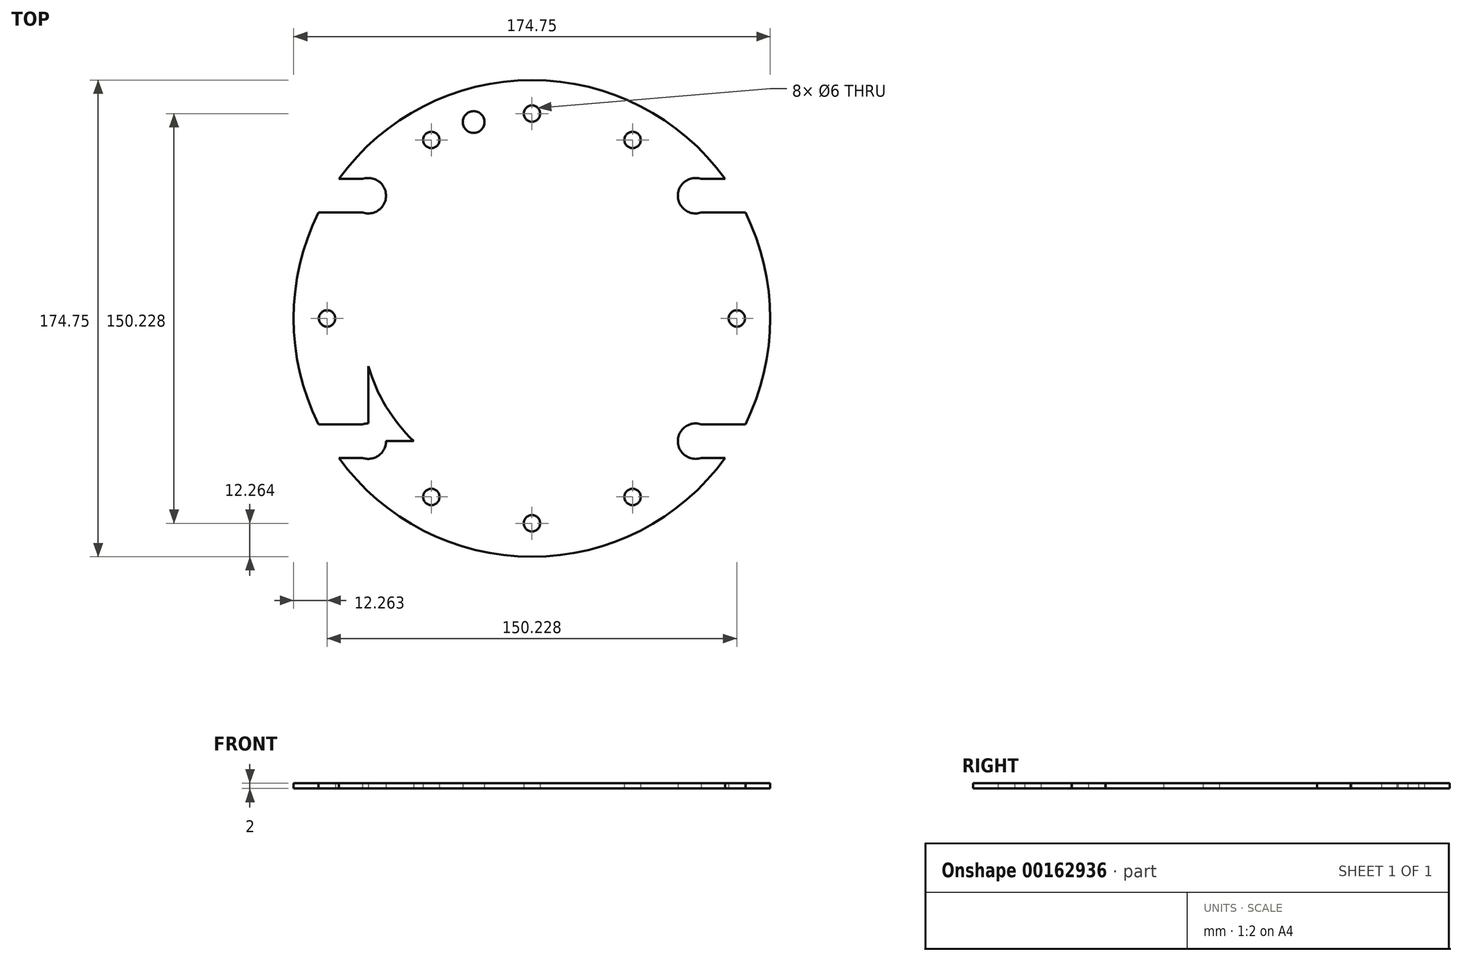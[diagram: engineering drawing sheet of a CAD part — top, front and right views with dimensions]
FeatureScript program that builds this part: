
annotation { "Feature Type Name" : "Feature", "Feature Type Description" : "" }
export const myFeature = defineFeature(function(context is Context, id is Id, definition is map)
    precondition{}
    {
        {
            var Q0;
            Q0=qCreatedBy(makeId("Top.planeOp"),FACE);
            var sketch = newSketch(context, id + "F0", { "sketchPlane" : qUnion([Q0])});
            skLineSegment(sketch, "E0.bottom", {"start": v(60.27, 43.84) * mm, "end": v(-59.73, 43.84) * mm});
            skLineSegment(sketch, "E0.top", {"start": v(60.27, -46.16) * mm, "end": v(-59.73, -46.16) * mm});
            skLineSegment(sketch, "E0.left", {"start": v(60.27, 43.84) * mm, "end": v(60.27, -46.16) * mm});
            skLineSegment(sketch, "E0.right", {"start": v(-59.73, 43.84) * mm, "end": v(-59.73, -46.16) * mm});
            skPoint(sketch, "E0.middle", {"position": v(0.27, -1.16) * mm});
            skCircle(sketch, "E1", {"center": v(60.27, 43.84) * mm, "radius": 6.5 * mm});
            skCircle(sketch, "E2", {"center": v(-59.73, 43.84) * mm, "radius": 6.5 * mm});
            skCircle(sketch, "E3", {"center": v(60.27, -46.16) * mm, "radius": 6.5 * mm});
            skCircle(sketch, "E4", {"center": v(-59.73, -46.16) * mm, "radius": 6.5 * mm});
            skCircle(sketch, "E5", {"center": v(0.27, -1.16) * mm, "radius": 87.38 * mm});
            skLineSegment(sketch, "E6.bottom", {"start": v(58.16, 49.99) * mm, "end": v(62.37, 49.99) * mm});
            skLineSegment(sketch, "E6.top", {"start": v(58.16, 37.69) * mm, "end": v(62.37, 37.69) * mm});
            skLineSegment(sketch, "E6.left", {"start": v(58.16, 49.99) * mm, "end": v(58.16, 37.69) * mm});
            skLineSegment(sketch, "E6.right", {"start": v(62.37, 49.99) * mm, "end": v(62.37, 37.69) * mm});
            skLineSegment(sketch, "E7.bottom", {"start": v(-61.84, 49.99) * mm, "end": v(-57.63, 49.99) * mm});
            skLineSegment(sketch, "E7.top", {"start": v(-61.84, 37.69) * mm, "end": v(-57.63, 37.69) * mm});
            skLineSegment(sketch, "E7.left", {"start": v(-61.84, 49.99) * mm, "end": v(-61.84, 37.69) * mm});
            skLineSegment(sketch, "E7.right", {"start": v(-57.63, 49.99) * mm, "end": v(-57.63, 37.69) * mm});
            skLineSegment(sketch, "E8.bottom", {"start": v(62.37, -40.01) * mm, "end": v(58.16, -40.01) * mm});
            skLineSegment(sketch, "E8.top", {"start": v(62.37, -52.31) * mm, "end": v(58.16, -52.31) * mm});
            skLineSegment(sketch, "E8.left", {"start": v(62.37, -40.01) * mm, "end": v(62.37, -52.31) * mm});
            skLineSegment(sketch, "E8.right", {"start": v(58.16, -40.01) * mm, "end": v(58.16, -52.31) * mm});
            skLineSegment(sketch, "E9.bottom", {"start": v(-61.84, -40.01) * mm, "end": v(-57.63, -40.01) * mm});
            skLineSegment(sketch, "E9.top", {"start": v(-61.84, -52.31) * mm, "end": v(-57.63, -52.31) * mm});
            skLineSegment(sketch, "E9.left", {"start": v(-61.84, -40.01) * mm, "end": v(-61.84, -52.31) * mm});
            skLineSegment(sketch, "E9.right", {"start": v(-57.63, -40.01) * mm, "end": v(-57.63, -52.31) * mm});
            skLineSegment(sketch, "E10.bottom", {"start": v(58.16, -40.01) * mm, "end": v(80.94, -40.01) * mm});
            skLineSegment(sketch, "E10.top", {"start": v(58.16, -52.31) * mm, "end": v(80.94, -52.31) * mm});
            skLineSegment(sketch, "E10.right", {"start": v(80.94, -40.01) * mm, "end": v(80.94, -52.31) * mm});
            skLineSegment(sketch, "E11.bottom", {"start": v(58.16, 49.99) * mm, "end": v(78.53, 49.99) * mm});
            skLineSegment(sketch, "E11.top", {"start": v(58.16, 37.69) * mm, "end": v(78.53, 37.69) * mm});
            skLineSegment(sketch, "E11.right", {"start": v(78.53, 49.99) * mm, "end": v(78.53, 37.69) * mm});
            skLineSegment(sketch, "E12.bottom", {"start": v(-57.63, 49.99) * mm, "end": v(-78, 49.99) * mm});
            skLineSegment(sketch, "E12.top", {"start": v(-57.63, 37.69) * mm, "end": v(-78, 37.69) * mm});
            skLineSegment(sketch, "E12.right", {"start": v(-78, 49.99) * mm, "end": v(-78, 37.69) * mm});
            skLineSegment(sketch, "E13.bottom", {"start": v(-57.63, -40.01) * mm, "end": v(-78, -40.01) * mm});
            skLineSegment(sketch, "E13.top", {"start": v(-57.63, -52.31) * mm, "end": v(-78, -52.31) * mm});
            skLineSegment(sketch, "E13.right", {"start": v(-78, -40.01) * mm, "end": v(-78, -52.31) * mm});
            skCircle(sketch, "E14", {"center": v(0.27, -1.16) * mm, "radius": 62.5 * mm});
            skCircle(sketch, "E15", {"center": v(0.27, 73.95) * mm, "radius": 3 * mm});
            skCircle(sketch, "E16", {"center": v(0.27, -76.28) * mm, "radius": 3 * mm});
            skCircle(sketch, "E17", {"center": v(75.38, -1.16) * mm, "radius": 3 * mm});
            skCircle(sketch, "E18", {"center": v(-74.85, -1.16) * mm, "radius": 3 * mm});
            skCircle(sketch, "E19", {"center": v(-21.11, 70.87) * mm, "radius": 4 * mm});
            skCircle(sketch, "E20", {"center": v(0.27, -1.16) * mm, "radius": 75.13 * mm});
            skLineSegment(sketch, "E21.bottom", {"start": v(37.16, 64.3) * mm, "end": v(-36.63, 64.3) * mm});
            skLineSegment(sketch, "E21.top", {"start": v(37.16, -66.61) * mm, "end": v(-36.63, -66.61) * mm});
            skLineSegment(sketch, "E21.left", {"start": v(37.16, 64.3) * mm, "end": v(37.16, -66.61) * mm});
            skLineSegment(sketch, "E21.right", {"start": v(-36.63, 64.3) * mm, "end": v(-36.63, -66.61) * mm});
            skCircle(sketch, "E22", {"center": v(-36.63, 64.3) * mm, "radius": 3 * mm});
            skCircle(sketch, "E23", {"center": v(37.16, 64.3) * mm, "radius": 3 * mm});
            skCircle(sketch, "E24", {"center": v(37.16, -66.61) * mm, "radius": 3 * mm});
            skCircle(sketch, "E25", {"center": v(-36.63, -66.61) * mm, "radius": 3 * mm});
            skSolve(sketch);
        }
        {
            var Q0;
            {var subQ0=sQuery(id+"F0.wireOp",EDGE,"E11.bottom");var subQ3=sQuery(id+"F0.wireOp",EDGE,"E5");var subQ4=makeQuery(id+"F0.imprint","INTERSECT",VERTEX,{"derivedFrom":[subQ3,subQ0]});Q0=makeQuery(id+"F0.imprint","IMPRINT",FACE,{"disambiguationData":[TD([[makeQuery(id+"F0.imprint","IMPRINT",EDGE,{"disambiguationData":[TD([[subQ4,-1.0]])],"derivedFrom":subQ3}),1.0]])]});}
            var Q1;
            {var subQ0=sQuery(id+"F0.wireOp",EDGE,"E20");var subQ1=sQuery(id+"F0.wireOp",EDGE,"E15");var subQ5=makeQuery(id+"F0.imprint","INTERSECT",VERTEX,{"disambiguationData":[OD(0.0)],"derivedFrom":[subQ1,subQ0]});Q1=makeQuery(id+"F0.imprint","IMPRINT",FACE,{"disambiguationData":[TD([[makeQuery(id+"F0.imprint","IMPRINT",EDGE,{"disambiguationData":[TD([[subQ5,1.0]])],"derivedFrom":subQ1}),-1.0]])]});}
            var Q2;
            {var subQ0=sQuery(id+"F0.wireOp",EDGE,"E21.left");var subQ1=sQuery(id+"F0.wireOp",EDGE,"E0.bottom");var subQ2=makeQuery(id+"F0.imprint","INTERSECT",VERTEX,{"derivedFrom":[subQ1,subQ0]});Q2=makeQuery(id+"F0.imprint","IMPRINT",FACE,{"disambiguationData":[TD([[makeQuery(id+"F0.imprint","IMPRINT",EDGE,{"disambiguationData":[TD([[subQ2,-1.0]])],"derivedFrom":subQ1}),-1.0]])]});}
            var Q3;
            {var subQ0=sQuery(id+"F0.wireOp",EDGE,"E21.left");var subQ1=sQuery(id+"F0.wireOp",EDGE,"E0.bottom");var subQ2=makeQuery(id+"F0.imprint","INTERSECT",VERTEX,{"derivedFrom":[subQ1,subQ0]});Q3=makeQuery(id+"F0.imprint","IMPRINT",FACE,{"disambiguationData":[TD([[makeQuery(id+"F0.imprint","IMPRINT",EDGE,{"disambiguationData":[TD([[subQ2,-1.0]])],"derivedFrom":subQ1}),1.0]])]});}
            var Q4;
            {var subQ0=sQuery(id+"F0.wireOp",EDGE,"E21.left");var subQ1=sQuery(id+"F0.wireOp",EDGE,"E14");var subQ2=makeQuery(id+"F0.imprint","INTERSECT",VERTEX,{"disambiguationData":[OD(0.0)],"derivedFrom":[subQ1,subQ0]});Q4=makeQuery(id+"F0.imprint","IMPRINT",FACE,{"disambiguationData":[TD([[makeQuery(id+"F0.imprint","IMPRINT",EDGE,{"disambiguationData":[TD([[subQ2,-1.0]])],"derivedFrom":subQ1}),-1.0]])]});}
            var Q5;
            {var subQ0=sQuery(id+"F0.wireOp",EDGE,"E14");var subQ1=sQuery(id+"F0.wireOp",EDGE,"E0.bottom");var subQ2=makeQuery(id+"F0.imprint","INTERSECT",VERTEX,{"disambiguationData":[OD(1.0)],"derivedFrom":[subQ1,subQ0]});Q5=makeQuery(id+"F0.imprint","IMPRINT",FACE,{"disambiguationData":[TD([[makeQuery(id+"F0.imprint","IMPRINT",EDGE,{"disambiguationData":[TD([[subQ2,-1.0]])],"derivedFrom":subQ1}),-1.0]])]});}
            var Q6;
            {var subQ0=sQuery(id+"F0.wireOp",EDGE,"E21.right");var subQ1=sQuery(id+"F0.wireOp",EDGE,"E0.bottom");var subQ2=makeQuery(id+"F0.imprint","INTERSECT",VERTEX,{"derivedFrom":[subQ1,subQ0]});Q6=makeQuery(id+"F0.imprint","IMPRINT",FACE,{"disambiguationData":[TD([[makeQuery(id+"F0.imprint","IMPRINT",EDGE,{"disambiguationData":[TD([[subQ2,-1.0]])],"derivedFrom":subQ1}),-1.0]])]});}
            var Q7;
            {var subQ1=sQuery(id+"F0.wireOp",EDGE,"E0.bottom");var subQ5=sQuery(id+"F0.wireOp",EDGE,"E21.right");var subQ6=makeQuery(id+"F0.imprint","INTERSECT",VERTEX,{"derivedFrom":[subQ1,subQ5]});Q7=makeQuery(id+"F0.imprint","IMPRINT",FACE,{"disambiguationData":[TD([[makeQuery(id+"F0.imprint","IMPRINT",EDGE,{"disambiguationData":[TD([[subQ6,-1.0]])],"derivedFrom":subQ1}),1.0]])]});}
            var Q8;
            {var subQ2=sQuery(id+"F0.wireOp",EDGE,"E0.bottom");var subQ6=sQuery(id+"F0.wireOp",EDGE,"E14");var subQ8=makeQuery(id+"F0.imprint","INTERSECT",VERTEX,{"disambiguationData":[OD(1.0)],"derivedFrom":[subQ2,subQ6]});Q8=makeQuery(id+"F0.imprint","IMPRINT",FACE,{"disambiguationData":[TD([[makeQuery(id+"F0.imprint","IMPRINT",EDGE,{"disambiguationData":[TD([[subQ8,-1.0]])],"derivedFrom":subQ2}),1.0]])]});}
            var Q9;
            {var subQ3=sQuery(id+"F0.wireOp",EDGE,"E0.right");var subQ5=sQuery(id+"F0.wireOp",EDGE,"E2");var subQ6=makeQuery(id+"F0.imprint","INTERSECT",VERTEX,{"derivedFrom":[subQ3,subQ5]});Q9=makeQuery(id+"F0.imprint","IMPRINT",FACE,{"disambiguationData":[TD([[makeQuery(id+"F0.imprint","IMPRINT",EDGE,{"disambiguationData":[TD([[subQ6,-1.0]])],"derivedFrom":subQ3}),-1.0]])]});}
            var Q10;
            {var subQ0=sQuery(id+"F0.wireOp",EDGE,"E13.right");var subQ1=sQuery(id+"F0.wireOp",EDGE,"E13.bottom");var subQ2=makeQuery(id+"F0.imprint","INTERSECT",VERTEX,{"derivedFrom":[subQ1,subQ0]});Q10=makeQuery(id+"F0.imprint","IMPRINT",FACE,{"disambiguationData":[TD([[makeQuery(id+"F0.imprint","IMPRINT",EDGE,{"disambiguationData":[TD([[subQ2,1.0]])],"derivedFrom":subQ1}),-1.0]])]});}
            var Q11;
            {var subQ0=sQuery(id+"F0.wireOp",EDGE,"E14");var subQ1=sQuery(id+"F0.wireOp",EDGE,"E0.right");var subQ2=makeQuery(id+"F0.imprint","INTERSECT",VERTEX,{"disambiguationData":[OD(0.0)],"derivedFrom":[subQ1,subQ0]});Q11=makeQuery(id+"F0.imprint","IMPRINT",FACE,{"disambiguationData":[TD([[makeQuery(id+"F0.imprint","IMPRINT",EDGE,{"disambiguationData":[TD([[subQ2,-1.0]])],"derivedFrom":subQ1}),-1.0]])]});}
            var Q12;
            {var subQ0=sQuery(id+"F0.wireOp",EDGE,"E14");var subQ1=sQuery(id+"F0.wireOp",EDGE,"E0.bottom");var subQ2=makeQuery(id+"F0.imprint","INTERSECT",VERTEX,{"disambiguationData":[OD(0.0)],"derivedFrom":[subQ1,subQ0]});Q12=makeQuery(id+"F0.imprint","IMPRINT",FACE,{"disambiguationData":[TD([[makeQuery(id+"F0.imprint","IMPRINT",EDGE,{"disambiguationData":[TD([[subQ2,-1.0]])],"derivedFrom":subQ1}),1.0]])]});}
            var Q13;
            {var subQ0=sQuery(id+"F0.wireOp",EDGE,"E14");var subQ1=sQuery(id+"F0.wireOp",EDGE,"E0.bottom");var subQ2=makeQuery(id+"F0.imprint","INTERSECT",VERTEX,{"disambiguationData":[OD(0.0)],"derivedFrom":[subQ1,subQ0]});Q13=makeQuery(id+"F0.imprint","IMPRINT",FACE,{"disambiguationData":[TD([[makeQuery(id+"F0.imprint","IMPRINT",EDGE,{"disambiguationData":[TD([[subQ2,-1.0]])],"derivedFrom":subQ1}),-1.0]])]});}
            var Q14;
            {var subQ1=sQuery(id+"F0.wireOp",EDGE,"E1");var subQ6=sQuery(id+"F0.wireOp",EDGE,"E0.bottom");var subQ10=makeQuery(id+"F0.imprint","INTERSECT",VERTEX,{"derivedFrom":[subQ6,subQ1]});Q14=makeQuery(id+"F0.imprint","IMPRINT",FACE,{"disambiguationData":[TD([[makeQuery(id+"F0.imprint","IMPRINT",EDGE,{"disambiguationData":[TD([[subQ10,-1.0]])],"derivedFrom":subQ6}),-1.0]])]});}
            var Q15;
            {var subQ0=sQuery(id+"F0.wireOp",EDGE,"E1");var subQ4=sQuery(id+"F0.wireOp",EDGE,"E0.bottom");var subQ5=makeQuery(id+"F0.imprint","INTERSECT",VERTEX,{"derivedFrom":[subQ4,subQ0]});Q15=makeQuery(id+"F0.imprint","IMPRINT",FACE,{"disambiguationData":[TD([[makeQuery(id+"F0.imprint","IMPRINT",EDGE,{"disambiguationData":[TD([[subQ5,-1.0]])],"derivedFrom":subQ4}),1.0]])]});}
            var Q16;
            {var subQ3=sQuery(id+"F0.wireOp",EDGE,"E0.left");var subQ6=sQuery(id+"F0.wireOp",EDGE,"E1");var subQ8=makeQuery(id+"F0.imprint","INTERSECT",VERTEX,{"derivedFrom":[subQ3,subQ6]});Q16=makeQuery(id+"F0.imprint","IMPRINT",FACE,{"disambiguationData":[TD([[makeQuery(id+"F0.imprint","IMPRINT",EDGE,{"disambiguationData":[TD([[subQ8,-1.0]])],"derivedFrom":subQ3}),1.0]])]});}
            var Q17;
            {var subQ5=sQuery(id+"F0.wireOp",EDGE,"E5");var subQ8=sQuery(id+"F0.wireOp",EDGE,"E10.bottom");var subQ9=makeQuery(id+"F0.imprint","INTERSECT",VERTEX,{"derivedFrom":[subQ5,subQ8]});Q17=makeQuery(id+"F0.imprint","IMPRINT",FACE,{"disambiguationData":[TD([[makeQuery(id+"F0.imprint","IMPRINT",EDGE,{"disambiguationData":[TD([[subQ9,1.0]])],"derivedFrom":subQ8}),1.0]])]});}
            var Q18;
            {var subQ0=sQuery(id+"F0.wireOp",EDGE,"E14");var subQ1=sQuery(id+"F0.wireOp",EDGE,"E0.left");var subQ2=makeQuery(id+"F0.imprint","INTERSECT",VERTEX,{"disambiguationData":[OD(0.0)],"derivedFrom":[subQ1,subQ0]});Q18=makeQuery(id+"F0.imprint","IMPRINT",FACE,{"disambiguationData":[TD([[makeQuery(id+"F0.imprint","IMPRINT",EDGE,{"disambiguationData":[TD([[subQ2,-1.0]])],"derivedFrom":subQ1}),1.0]])]});}
            var Q19;
            {var subQ13=sQuery(id+"F0.wireOp",EDGE,"E13.top");var subQ15=sQuery(id+"F0.wireOp",EDGE,"E5");var subQ16=makeQuery(id+"F0.imprint","INTERSECT",VERTEX,{"derivedFrom":[subQ15,subQ13]});Q19=makeQuery(id+"F0.imprint","IMPRINT",FACE,{"disambiguationData":[TD([[makeQuery(id+"F0.imprint","IMPRINT",EDGE,{"disambiguationData":[TD([[subQ16,-1.0]])],"derivedFrom":subQ15}),1.0]])]});}
            var Q20;
            {var subQ5=sQuery(id+"F0.wireOp",EDGE,"E20");var subQ7=sQuery(id+"F0.wireOp",EDGE,"E16");var subQ10=makeQuery(id+"F0.imprint","INTERSECT",VERTEX,{"disambiguationData":[OD(0.0)],"derivedFrom":[subQ7,subQ5]});Q20=makeQuery(id+"F0.imprint","IMPRINT",FACE,{"disambiguationData":[TD([[makeQuery(id+"F0.imprint","IMPRINT",EDGE,{"disambiguationData":[TD([[subQ10,1.0]])],"derivedFrom":subQ7}),-1.0]])]});}
            var Q21;
            {var subQ1=sQuery(id+"F0.wireOp",EDGE,"E14");var subQ5=sQuery(id+"F0.wireOp",EDGE,"E21.right");var subQ6=makeQuery(id+"F0.imprint","INTERSECT",VERTEX,{"disambiguationData":[OD(1.0)],"derivedFrom":[subQ1,subQ5]});Q21=makeQuery(id+"F0.imprint","IMPRINT",FACE,{"disambiguationData":[TD([[makeQuery(id+"F0.imprint","IMPRINT",EDGE,{"disambiguationData":[TD([[subQ6,-1.0]])],"derivedFrom":subQ1}),-1.0]])]});}
            var Q22;
            {var subQ0=sQuery(id+"F0.wireOp",EDGE,"E21.left");var subQ1=sQuery(id+"F0.wireOp",EDGE,"E0.top");var subQ2=makeQuery(id+"F0.imprint","INTERSECT",VERTEX,{"derivedFrom":[subQ1,subQ0]});Q22=makeQuery(id+"F0.imprint","IMPRINT",FACE,{"disambiguationData":[TD([[makeQuery(id+"F0.imprint","IMPRINT",EDGE,{"disambiguationData":[TD([[subQ2,-1.0]])],"derivedFrom":subQ1}),1.0]])]});}
            var Q23;
            {var subQ0=sQuery(id+"F0.wireOp",EDGE,"E14");var subQ1=sQuery(id+"F0.wireOp",EDGE,"E0.top");var subQ2=makeQuery(id+"F0.imprint","INTERSECT",VERTEX,{"disambiguationData":[OD(0.0)],"derivedFrom":[subQ1,subQ0]});Q23=makeQuery(id+"F0.imprint","IMPRINT",FACE,{"disambiguationData":[TD([[makeQuery(id+"F0.imprint","IMPRINT",EDGE,{"disambiguationData":[TD([[subQ2,-1.0]])],"derivedFrom":subQ1}),1.0]])]});}
            var Q24;
            {var subQ0=sQuery(id+"F0.wireOp",EDGE,"E21.right");var subQ1=sQuery(id+"F0.wireOp",EDGE,"E0.top");var subQ2=makeQuery(id+"F0.imprint","INTERSECT",VERTEX,{"derivedFrom":[subQ1,subQ0]});Q24=makeQuery(id+"F0.imprint","IMPRINT",FACE,{"disambiguationData":[TD([[makeQuery(id+"F0.imprint","IMPRINT",EDGE,{"disambiguationData":[TD([[subQ2,-1.0]])],"derivedFrom":subQ1}),1.0]])]});}
            var Q25;
            {var subQ2=sQuery(id+"F0.wireOp",EDGE,"E0.top");var subQ6=sQuery(id+"F0.wireOp",EDGE,"E14");var subQ8=makeQuery(id+"F0.imprint","INTERSECT",VERTEX,{"disambiguationData":[OD(1.0)],"derivedFrom":[subQ2,subQ6]});Q25=makeQuery(id+"F0.imprint","IMPRINT",FACE,{"disambiguationData":[TD([[makeQuery(id+"F0.imprint","IMPRINT",EDGE,{"disambiguationData":[TD([[subQ8,-1.0]])],"derivedFrom":subQ2}),-1.0]])]});}
            var Q26;
            {var subQ0=sQuery(id+"F0.wireOp",EDGE,"E14");var subQ1=sQuery(id+"F0.wireOp",EDGE,"E0.top");var subQ2=makeQuery(id+"F0.imprint","INTERSECT",VERTEX,{"disambiguationData":[OD(1.0)],"derivedFrom":[subQ1,subQ0]});Q26=makeQuery(id+"F0.imprint","IMPRINT",FACE,{"disambiguationData":[TD([[makeQuery(id+"F0.imprint","IMPRINT",EDGE,{"disambiguationData":[TD([[subQ2,-1.0]])],"derivedFrom":subQ1}),1.0]])]});}
            var Q27;
            {var subQ0=sQuery(id+"F0.wireOp",EDGE,"E3");var subQ2=sQuery(id+"F0.wireOp",EDGE,"E0.top");var subQ3=makeQuery(id+"F0.imprint","INTERSECT",VERTEX,{"derivedFrom":[subQ2,subQ0]});Q27=makeQuery(id+"F0.imprint","IMPRINT",FACE,{"disambiguationData":[TD([[makeQuery(id+"F0.imprint","IMPRINT",EDGE,{"disambiguationData":[TD([[subQ3,-1.0]])],"derivedFrom":subQ2}),-1.0]])]});}
            var Q28;
            {var subQ1=sQuery(id+"F0.wireOp",EDGE,"E3");var subQ6=sQuery(id+"F0.wireOp",EDGE,"E0.top");var subQ10=makeQuery(id+"F0.imprint","INTERSECT",VERTEX,{"derivedFrom":[subQ6,subQ1]});Q28=makeQuery(id+"F0.imprint","IMPRINT",FACE,{"disambiguationData":[TD([[makeQuery(id+"F0.imprint","IMPRINT",EDGE,{"disambiguationData":[TD([[subQ10,-1.0]])],"derivedFrom":subQ6}),1.0]])]});}
            extrude(context, id + "F1", {"entities" : qUnion([Q0, Q1, Q2, Q3, Q4, Q5, Q6, Q7, Q8, Q9, Q10, Q11, Q12, Q13, Q14, Q15, Q16, Q17, Q18, Q19, Q20, Q21, Q22, Q23, Q24, Q25, Q26, Q27, Q28]), "depth" : 2 * mm});
        }
    });
